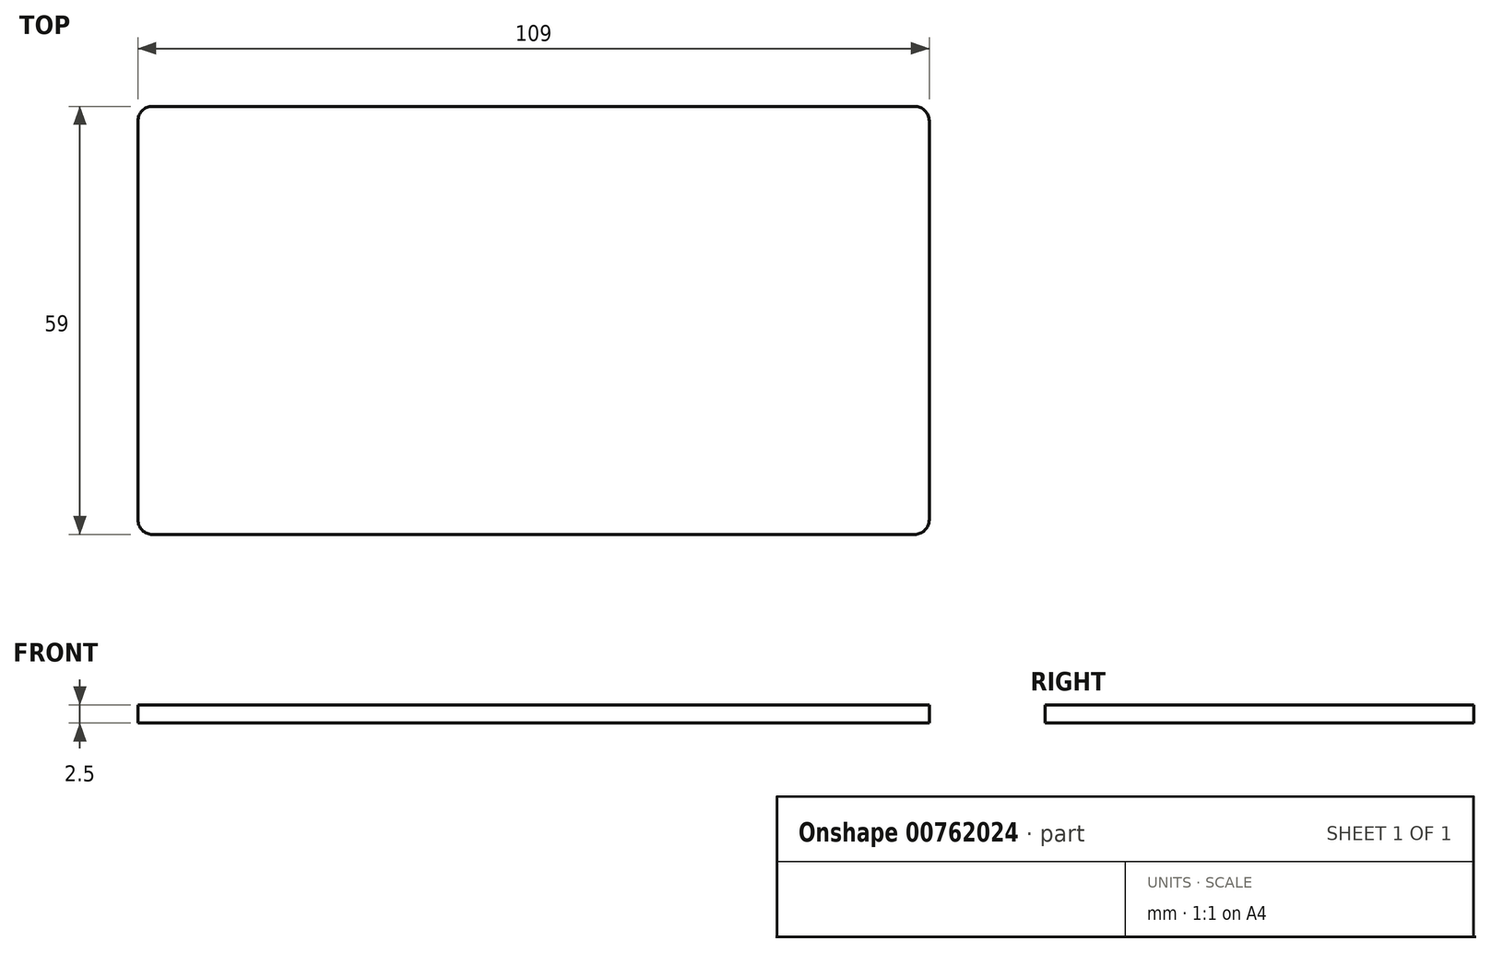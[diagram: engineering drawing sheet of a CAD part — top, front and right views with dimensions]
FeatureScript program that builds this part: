
annotation { "Feature Type Name" : "Feature", "Feature Type Description" : "" }
export const myFeature = defineFeature(function(context is Context, id is Id, definition is map)
    precondition{}
    {
        {
            var Q0;
            Q0=qCreatedBy(makeId("Top.planeOp"),FACE);
            var sketch = newSketch(context, id + "F0", { "sketchPlane" : qUnion([Q0])});
            skLineSegment(sketch, "E0.bottom", {"start": v(2, 0) * mm, "end": v(107, 0) * mm});
            skLineSegment(sketch, "E0.top", {"start": v(2, 59) * mm, "end": v(107, 59) * mm});
            skLineSegment(sketch, "E0.left", {"start": v(0, 2) * mm, "end": v(0, 57) * mm});
            skLineSegment(sketch, "E0.right", {"start": v(109, 2) * mm, "end": v(109, 57) * mm});
            skPoint(sketch, "E1.visualSharp", {"position": v(109, 59) * mm});
            skArc(sketch, "E1.filletArc", {"start": v(109, 57) * mm, "mid": v(108.41, 58.41) * mm, "end": v(107, 59) * mm});
            skPoint(sketch, "E2.visualSharp", {"position": v(109, 0) * mm});
            skArc(sketch, "E2.filletArc", {"start": v(107, 0) * mm, "mid": v(108.41, 0.59) * mm, "end": v(109, 2) * mm});
            skPoint(sketch, "E3.visualSharp", {"position": v(0, 0) * mm});
            skArc(sketch, "E3.filletArc", {"start": v(0, 2) * mm, "mid": v(0.59, 0.59) * mm, "end": v(2, 0) * mm});
            skPoint(sketch, "E4.visualSharp", {"position": v(0, 59) * mm});
            skArc(sketch, "E4.filletArc", {"start": v(2, 59) * mm, "mid": v(0.59, 58.41) * mm, "end": v(0, 57) * mm});
            skSolve(sketch);
        }
        {
            var Q0;
            Q0 = qSketchRegion(id + "F0", true);
            extrude(context, id + "F1", {"entities" : qUnion([Q0]), "depth" : 2.5 * mm, "offsetDistance" : 25 * mm});
        }
    });
